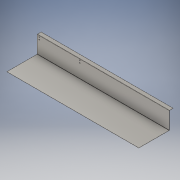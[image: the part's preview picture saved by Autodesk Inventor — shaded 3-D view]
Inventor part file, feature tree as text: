
AUTODESK INVENTOR PART (.ipt)
format: ipt  version: 2016 (Build 200138000, 138)  size: 186,368 bytes
history: native  units: mm
features: sheet_metal_op x7, sketch x4, other x4, hole x1
ambient origin geometry x8: Origin, YZ Plane, XZ Plane, XY Plane, X Axis, Y Axis, Z Axis, Center Point
bodies: Solid1 (feature_tree)
feature tree (16):
  sheet_metal_op  "Face1"
  sheet_metal_op  "Flange1"
  sheet_metal_op  "Flange2"
  hole  "Hole1"  [1 undecoded]
  sketch  "Sketch1"  dims[d0=392.0mm d1=1695.0mm]
  other  "Plate1"
  sketch  "Sketch2"  dims[d2=1.6mm]
  other  "Plate2"
  sheet_metal_op  "Bend1"
  sheet_metal_op  "Corner1"
  sketch  "Sketch3"  dims[d3=1.6mm]
  other  "Plate3"
  sheet_metal_op  "Bend2"
  sheet_metal_op  "Corner2"
  sketch  "Sketch4"  dims[d4=0.8mm d5=3.2mm d6=1.6mm d7=223.0mm d8=90.0deg d9=1.6mm d10=6.4mm d11=1.6mm d12=1.6mm d13=1.6mm d14=0.8mm d15=3.2mm d16=1.6mm d17=50.0mm d18=-15.707963mm d19=1.6mm d20=6.4mm d21=1.6mm d22=1.6mm d23=60.0mm d24=12.0mm d25=12.0mm d26=25.0mm d27=25.0mm d28=15.0mm d29=15.0mm d30=12.0mm d31=12.0mm d34=12.0mm d35=6.0mm d36=4.0mm d37=2.0mm d38=90.0deg d39=1.6mm d40=20.594885mm d41=570.0mm d42=15.0mm d43=15.0mm d44=25.0mm d45=25.0mm]
  other  "Definition1"
note: 1 required parameter value undecoded (feature->parameter linkage not recoverable at this tier; creation-order binding heuristic only, values carry confidence <= 0.55)
